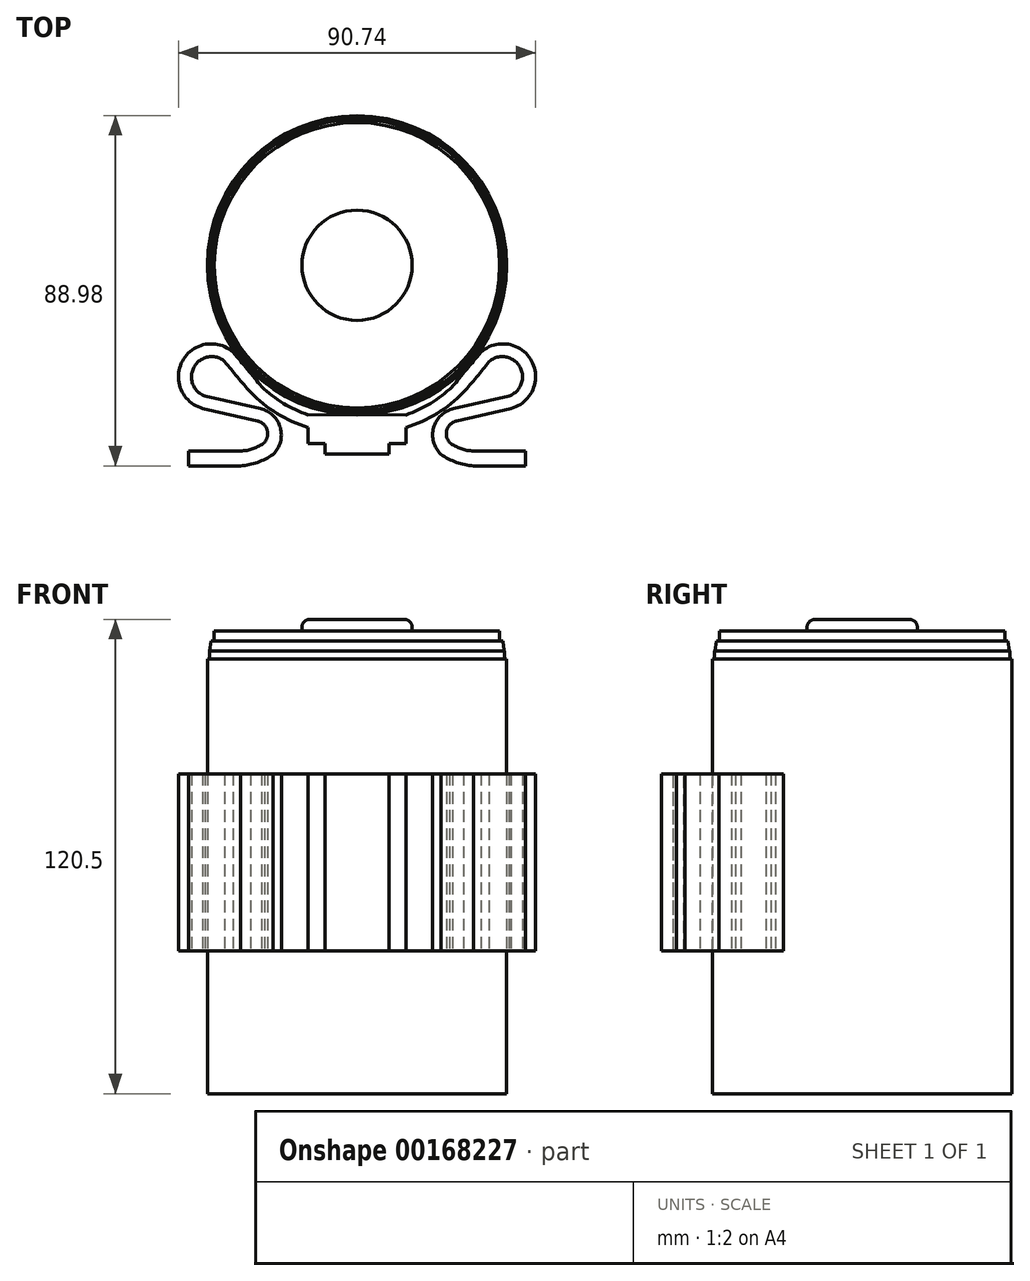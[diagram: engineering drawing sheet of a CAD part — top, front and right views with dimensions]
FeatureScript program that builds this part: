
annotation { "Feature Type Name" : "Feature", "Feature Type Description" : "" }
export const myFeature = defineFeature(function(context is Context, id is Id, definition is map)
    precondition{}
    {
        {
            var Q0;
            Q0=qCreatedBy(makeId("Top.planeOp"),FACE);
            var sketch = newSketch(context, id + "F0", { "sketchPlane" : qUnion([Q0])});
            skLineSegment(sketch, "E0", {"start": v(-45, 31.85) * mm, "end": v(-45, -23.43) * mm, "construction": true});
            skLineSegment(sketch, "E1", {"start": v(45, 35.82) * mm, "end": v(45, -24.86) * mm, "construction": true});
            skLineSegment(sketch, "E2", {"start": v(0, 45.7) * mm, "end": v(0, -31.06) * mm, "construction": true});
            skLineSegment(sketch, "E3", {"start": v(-42.56, 0.72) * mm, "end": v(-29.8, 0.72) * mm});
            skLineSegment(sketch, "E4", {"start": v(-29.8, 0.72) * mm, "end": v(-29.8, 1.26) * mm});
            skLineSegment(sketch, "E5", {"start": v(-29.8, 1.26) * mm, "end": v(-24.48, 2.8) * mm});
            skLineSegment(sketch, "E6", {"start": v(-24.47, 15.44) * mm, "end": v(-38.8, 18.71) * mm});
            skLineSegment(sketch, "E7", {"start": v(-33.58, 27.47) * mm, "end": v(-31.38, 25.18) * mm});
            skLineSegment(sketch, "E8", {"start": v(-3.53, 9.3) * mm, "end": v(0, 9.32) * mm});
            skLineSegment(sketch, "E9", {"start": v(-42.56, 0.72) * mm, "end": v(-42.4, 5.06) * mm});
            skLineSegment(sketch, "E10", {"start": v(-29.62, 4.65) * mm, "end": v(-25.37, 5.88) * mm});
            skLineSegment(sketch, "E11", {"start": v(-25.37, 12.36) * mm, "end": v(-39.82, 15.66) * mm});
            skLineSegment(sketch, "E12", {"start": v(-31.4, 29.83) * mm, "end": v(-29.25, 27.58) * mm});
            skLineSegment(sketch, "E13", {"start": v(-5.2, 12.4) * mm, "end": v(0, 12.4) * mm});
            skLineSegment(sketch, "E14", {"start": v(0, 12.4) * mm, "end": v(0, 9.32) * mm});
            skPoint(sketch, "E14.endSnap0", {"position": v(0, 9.32) * mm});
            skPoint(sketch, "E15.orphan", {"position": v(3.53, 9.32) * mm});
            skLineSegment(sketch, "E16", {"start": v(-29.62, 4.65) * mm, "end": v(-42.4, 5.06) * mm});
            skPoint(sketch, "E17.visualSharp", {"position": v(-24.47, 2.8) * mm});
            skArc(sketch, "E18", {"start": v(-24.47, 2.8) * mm, "mid": v(-19.43, 9.12) * mm, "end": v(-24.47, 15.44) * mm});
            skArc(sketch, "E19", {"start": v(-25.37, 5.88) * mm, "mid": v(-22.63, 9.12) * mm, "end": v(-25.37, 12.36) * mm});
            skArc(sketch, "E20", {"start": v(-33.58, 27.47) * mm, "mid": v(-41.4, 26.2) * mm, "end": v(-38.8, 18.71) * mm});
            skArc(sketch, "E21", {"start": v(-31.4, 29.83) * mm, "mid": v(-44.17, 27.83) * mm, "end": v(-39.82, 15.66) * mm});
            skArc(sketch, "E22", {"start": v(-31.38, 25.18) * mm, "mid": v(-19.45, 13.74) * mm, "end": v(-3.53, 9.3) * mm});
            skArc(sketch, "E23", {"start": v(-29.25, 27.58) * mm, "mid": v(-19.08, 17.04) * mm, "end": v(-5.2, 12.4) * mm});
            skLineSegment(sketch, "E24", {"start": v(-72.69, 0) * mm, "end": v(55.3, 0) * mm, "construction": true});
            skLineSegment(sketch, "E25.MirrorCS", {"start": v(5.2, 12.4) * mm, "end": v(0, 12.4) * mm});
            skLineSegment(sketch, "E26.MirrorCS", {"start": v(3.53, 9.3) * mm, "end": v(0, 9.32) * mm});
            skArc(sketch, "E27.MirrorCS", {"start": v(31.38, 25.18) * mm, "mid": v(19.45, 13.74) * mm, "end": v(3.53, 9.3) * mm});
            skArc(sketch, "E28.MirrorCS", {"start": v(29.25, 27.58) * mm, "mid": v(19.08, 17.04) * mm, "end": v(5.2, 12.4) * mm});
            skLineSegment(sketch, "E29.MirrorCS", {"start": v(31.4, 29.83) * mm, "end": v(29.25, 27.58) * mm});
            skLineSegment(sketch, "E30.MirrorCS", {"start": v(33.58, 27.47) * mm, "end": v(31.38, 25.18) * mm});
            skArc(sketch, "E31.MirrorCS", {"start": v(31.4, 29.83) * mm, "mid": v(44.17, 27.83) * mm, "end": v(39.82, 15.66) * mm});
            skArc(sketch, "E32.MirrorCS", {"start": v(33.58, 27.47) * mm, "mid": v(41.4, 26.2) * mm, "end": v(38.8, 18.71) * mm});
            skLineSegment(sketch, "E33.MirrorCS", {"start": v(24.47, 15.44) * mm, "end": v(38.8, 18.71) * mm});
            skLineSegment(sketch, "E34.MirrorCS", {"start": v(25.37, 12.36) * mm, "end": v(39.82, 15.66) * mm});
            skArc(sketch, "E35.MirrorCS", {"start": v(25.37, 5.88) * mm, "mid": v(22.63, 9.12) * mm, "end": v(25.37, 12.36) * mm});
            skArc(sketch, "E36.MirrorCS", {"start": v(24.47, 2.8) * mm, "mid": v(19.43, 9.12) * mm, "end": v(24.47, 15.44) * mm});
            skLineSegment(sketch, "E37.MirrorCS", {"start": v(29.8, 1.26) * mm, "end": v(24.48, 2.8) * mm});
            skLineSegment(sketch, "E38.MirrorCS", {"start": v(29.62, 4.65) * mm, "end": v(25.37, 5.88) * mm});
            skLineSegment(sketch, "E39.MirrorCS", {"start": v(29.62, 4.65) * mm, "end": v(42.4, 5.06) * mm});
            skLineSegment(sketch, "E40.MirrorCS", {"start": v(42.56, 0.72) * mm, "end": v(42.4, 5.06) * mm});
            skLineSegment(sketch, "E41.MirrorCS", {"start": v(42.56, 0.72) * mm, "end": v(29.8, 0.72) * mm});
            skLineSegment(sketch, "E42.MirrorCS", {"start": v(29.8, 0.72) * mm, "end": v(29.8, 1.26) * mm});
            skSolve(sketch);
        }
        {
            var Q0;
            Q0=qCreatedBy(makeId("Top.planeOp"),FACE);
            var sketch = newSketch(context, id + "F1", { "sketchPlane" : qUnion([Q0])});
            skLineSegment(sketch, "E43.bottom", {"start": v(-42.76, 0.96) * mm, "end": v(-29.61, 0.96) * mm});
            skLineSegment(sketch, "E43.top", {"start": v(-42.76, 4.77) * mm, "end": v(-29.61, 4.77) * mm});
            skLineSegment(sketch, "E43.left", {"start": v(-42.76, 0.96) * mm, "end": v(-42.76, 4.77) * mm});
            skArc(sketch, "E44", {"start": v(-23.5, 6.93) * mm, "mid": v(-22.86, 10.17) * mm, "end": v(-25.3, 12.4) * mm});
            skArc(sketch, "E45", {"start": v(-21.32, 3.9) * mm, "mid": v(-19.47, 10.68) * mm, "end": v(-24.56, 15.52) * mm});
            skLineSegment(sketch, "E46", {"start": v(-24.56, 15.52) * mm, "end": v(-38.6, 18.7) * mm});
            skLineSegment(sketch, "E47", {"start": v(-25.3, 12.4) * mm, "end": v(-39.18, 15.57) * mm});
            skArc(sketch, "E48", {"start": v(-29.61, 0.96) * mm, "mid": v(-25.26, 1.86) * mm, "end": v(-21.32, 3.9) * mm});
            skArc(sketch, "E49", {"start": v(-29.61, 4.77) * mm, "mid": v(-26.37, 5.33) * mm, "end": v(-23.5, 6.93) * mm});
            skArc(sketch, "E50", {"start": v(-33.6, 27.5) * mm, "mid": v(-41.39, 26.11) * mm, "end": v(-38.6, 18.7) * mm});
            skArc(sketch, "E51", {"start": v(-31.47, 29.85) * mm, "mid": v(-44.37, 27.59) * mm, "end": v(-39.18, 15.57) * mm});
            skArc(sketch, "E52", {"start": v(-24.2, 21.1) * mm, "mid": v(-27.82, 25.49) * mm, "end": v(-31.47, 29.85) * mm});
            skArc(sketch, "E53", {"start": v(-33.6, 27.5) * mm, "mid": v(-30.4, 23.53) * mm, "end": v(-27.05, 19.68) * mm});
            skArc(sketch, "E54", {"start": v(-24.2, 21.1) * mm, "mid": v(-13.04, 14.14) * mm, "end": v(0, 12.41) * mm});
            skArc(sketch, "E55", {"start": v(-27.05, 19.68) * mm, "mid": v(-14.68, 11.48) * mm, "end": v(0, 9.32) * mm});
            skLineSegment(sketch, "E56.0", {"start": v(0, 45.7) * mm, "end": v(0, -31.06) * mm, "construction": true});
            skArc(sketch, "E57.MirrorCS", {"start": v(23.5, 6.93) * mm, "mid": v(22.86, 10.17) * mm, "end": v(25.3, 12.4) * mm});
            skArc(sketch, "E58.MirrorCS", {"start": v(31.47, 29.85) * mm, "mid": v(44.37, 27.59) * mm, "end": v(39.18, 15.57) * mm});
            skArc(sketch, "E59.MirrorCS", {"start": v(24.2, 21.1) * mm, "mid": v(13.04, 14.14) * mm, "end": v(0, 12.41) * mm});
            skLineSegment(sketch, "E60.MirrorCS", {"start": v(24.56, 15.52) * mm, "end": v(38.6, 18.7) * mm});
            skArc(sketch, "E61.MirrorCS", {"start": v(24.2, 21.1) * mm, "mid": v(27.82, 25.49) * mm, "end": v(31.47, 29.85) * mm});
            skArc(sketch, "E62.MirrorCS", {"start": v(33.6, 27.5) * mm, "mid": v(41.39, 26.11) * mm, "end": v(38.6, 18.7) * mm});
            skArc(sketch, "E63.MirrorCS", {"start": v(27.05, 19.68) * mm, "mid": v(14.68, 11.48) * mm, "end": v(0, 9.32) * mm});
            skArc(sketch, "E64.MirrorCS", {"start": v(21.32, 3.9) * mm, "mid": v(19.47, 10.68) * mm, "end": v(24.56, 15.52) * mm});
            skArc(sketch, "E65.MirrorCS", {"start": v(29.61, 4.77) * mm, "mid": v(26.37, 5.33) * mm, "end": v(23.5, 6.93) * mm});
            skArc(sketch, "E66.MirrorCS", {"start": v(33.6, 27.5) * mm, "mid": v(30.4, 23.53) * mm, "end": v(27.05, 19.68) * mm});
            skLineSegment(sketch, "E67.MirrorCS", {"start": v(25.3, 12.4) * mm, "end": v(39.18, 15.57) * mm});
            skArc(sketch, "E68.MirrorCS", {"start": v(29.61, 0.96) * mm, "mid": v(25.26, 1.86) * mm, "end": v(21.32, 3.9) * mm});
            skLineSegment(sketch, "E69.MirrorCS", {"start": v(42.76, 4.77) * mm, "end": v(29.61, 4.77) * mm});
            skLineSegment(sketch, "E70.MirrorCS", {"start": v(42.76, 0.96) * mm, "end": v(29.61, 0.96) * mm});
            skLineSegment(sketch, "E71.MirrorCS", {"start": v(42.76, 0.96) * mm, "end": v(42.76, 4.77) * mm});
            skSolve(sketch);
        }
        {
            var Q0;
            Q0 = qSketchRegion(id + "F1", true);
            extrude(context, id + "F2", {"entities" : qUnion([Q0]), "depth" : 45 * mm});
        }
        {
            var Q0;
            Q0=qCreatedBy(makeId("Top.planeOp"),FACE);
            cPlane(context, id + "F3", {"entities" : qUnion([Q0]), "cplaneType" : CPlaneType.OFFSET, "offset" : 19 * mm, "width" : 150 * mm, "height" : 150 * mm});
        }
        {
            var Q0;
            Q0=qCreatedBy(id+"F3.planeOp",FACE);
            var sketch = newSketch(context, id + "F4", { "sketchPlane" : qUnion([Q0])});
            skCircle(sketch, "E72", {"center": v(0, 51.94) * mm, "radius": 38 * mm});
            skSolve(sketch);
        }
        {
            var Q0;
            Q0 = qSketchRegion(id + "F4", true);
            extrude(context, id + "F5", {"entities" : qUnion([Q0]), "endBound" : BoundingType.SYMMETRIC, "depth" : 110.5 * mm});
        }
        {
            var Q0;
            Q0=makeQuery(id+"F2.opExtrude","CAP_FACE",FACE,{"disambiguationData":[OSD([sQuery(id+"F1.wireOp",EDGE,"E43.bottom"),sQuery(id+"F1.wireOp",EDGE,"E43.top"),sQuery(id+"F1.wireOp",EDGE,"E43.left"),sQuery(id+"F1.wireOp",EDGE,"E44"),sQuery(id+"F1.wireOp",EDGE,"E45"),sQuery(id+"F1.wireOp",EDGE,"E46"),sQuery(id+"F1.wireOp",EDGE,"E47"),sQuery(id+"F1.wireOp",EDGE,"E48"),sQuery(id+"F1.wireOp",EDGE,"E49"),sQuery(id+"F1.wireOp",EDGE,"E50"),sQuery(id+"F1.wireOp",EDGE,"E51"),sQuery(id+"F1.wireOp",EDGE,"E52"),sQuery(id+"F1.wireOp",EDGE,"E53"),sQuery(id+"F1.wireOp",EDGE,"E54"),sQuery(id+"F1.wireOp",EDGE,"E55"),sQuery(id+"F1.wireOp",EDGE,"E58.MirrorCS"),sQuery(id+"F1.wireOp",EDGE,"E59.MirrorCS"),sQuery(id+"F1.wireOp",EDGE,"E60.MirrorCS"),sQuery(id+"F1.wireOp",EDGE,"E61.MirrorCS"),sQuery(id+"F1.wireOp",EDGE,"E62.MirrorCS"),sQuery(id+"F1.wireOp",EDGE,"E63.MirrorCS"),sQuery(id+"F1.wireOp",EDGE,"E66.MirrorCS"),sQuery(id+"F1.wireOp",EDGE,"E67.MirrorCS"),sQuery(id+"F1.wireOp",EDGE,"E64.MirrorCS"),sQuery(id+"F1.wireOp",EDGE,"E68.MirrorCS"),sQuery(id+"F1.wireOp",EDGE,"E69.MirrorCS"),sQuery(id+"F1.wireOp",EDGE,"E65.MirrorCS"),sQuery(id+"F1.wireOp",EDGE,"E70.MirrorCS"),sQuery(id+"F1.wireOp",EDGE,"E71.MirrorCS"),sQuery(id+"F1.wireOp",EDGE,"E57.MirrorCS")])],"isStart":false});
            var sketch = newSketch(context, id + "F6", { "sketchPlane" : qUnion([Q0])});
            skLineSegment(sketch, "E73.bottom", {"start": v(12.43, 13.93) * mm, "end": v(-12.43, 13.95) * mm});
            skLineSegment(sketch, "E73.left", {"start": v(12.43, 13.93) * mm, "end": v(12.43, 6.69) * mm});
            skLineSegment(sketch, "E73.right", {"start": v(-12.43, 13.95) * mm, "end": v(-12.43, 6.69) * mm});
            skPoint(sketch, "E73.middle", {"position": v(0, 9.32) * mm});
            skLineSegment(sketch, "E74", {"start": v(-12.43, 6.69) * mm, "end": v(-8.18, 6.69) * mm});
            skPoint(sketch, "E75.orphan", {"position": v(-12.43, 4.7) * mm});
            skPoint(sketch, "E76.orphan", {"position": v(12.43, 4.68) * mm});
            skLineSegment(sketch, "E77.left", {"start": v(8.18, 4.03) * mm, "end": v(8.18, 6.69) * mm});
            skLineSegment(sketch, "E77.right", {"start": v(-8.18, 4.03) * mm, "end": v(-8.18, 6.69) * mm});
            skPoint(sketch, "E77.middle", {"position": v(0, 7.03) * mm});
            skLineSegment(sketch, "E78.trimOffspring", {"start": v(8.18, 6.69) * mm, "end": v(12.43, 6.69) * mm});
            skPoint(sketch, "E77.top.end.orphan", {"position": v(-8.18, 10.03) * mm});
            skPoint(sketch, "E79.orphan", {"position": v(8.18, 10.03) * mm});
            skLineSegment(sketch, "E80", {"start": v(-8.18, 4.03) * mm, "end": v(8.18, 4.03) * mm});
            skSolve(sketch);
        }
        {
            var Q0;
            Q0 = qSketchRegion(id + "F6", true);
            extrude(context, id + "F7", {"entities" : qUnion([Q0]), "operationType" : NewBodyOperationType.ADD, "oppositeDirection" : true, "depth" : 45 * mm});
        }
        {
            var Q0;
            Q0=makeQuery(id+"F5.opExtrude","CAP_FACE",FACE,{"disambiguationData":[OSD([sQuery(id+"F4.wireOp",EDGE,"E72")])],"isStart":false});
            var sketch = newSketch(context, id + "F8", { "sketchPlane" : qUnion([Q0])});
            skCircle(sketch, "E81", {"center": v(0, 51.94) * mm, "radius": 37.5 * mm});
            skSolve(sketch);
        }
        {
            var Q0;
            Q0 = qSketchRegion(id + "F8", true);
            extrude(context, id + "F9", {"entities" : qUnion([Q0]), "depth" : 2 * mm});
        }
        {
            var Q0;
            Q0=makeQuery(id+"F9.opExtrude","CAP_FACE",FACE,{"disambiguationData":[OSD([sQuery(id+"F8.wireOp",EDGE,"E81")])],"isStart":false});
            var sketch = newSketch(context, id + "F10", { "sketchPlane" : qUnion([Q0])});
            skCircle(sketch, "E82", {"center": v(0, 51.94) * mm, "radius": 37.4 * mm});
            skSolve(sketch);
        }
        {
            var Q0;
            Q0 = qSketchRegion(id + "F10", true);
            extrude(context, id + "F11", {"entities" : qUnion([Q0]), "operationType" : NewBodyOperationType.ADD, "depth" : 2.5 * mm, "hasDraft" : true, "draftAngle" : 8 * degree, "draftPullDirection" : true, "hasSecondDirection" : true, "secondDirectionOppositeDirection" : true, "secondDirectionDepth" : 25 * mm});
        }
        {
            var Q0;
            Q0=makeQuery(id+"F11.opExtrude","CAP_FACE",FACE,{"disambiguationData":[OSD([sQuery(id+"F10.wireOp",EDGE,"E82")])],"isStart":false});
            var sketch = newSketch(context, id + "F12", { "sketchPlane" : qUnion([Q0])});
            skCircle(sketch, "E83", {"center": v(0, 51.94) * mm, "radius": 36.25 * mm});
            skSolve(sketch);
        }
        {
            var Q0;
            Q0 = qSketchRegion(id + "F12", true);
            extrude(context, id + "F13", {"entities" : qUnion([Q0]), "operationType" : NewBodyOperationType.ADD, "depth" : 2.5 * mm});
        }
        {
            var Q0;
            Q0=makeQuery(id+"F13.opExtrude","CAP_FACE",FACE,{"disambiguationData":[OSD([sQuery(id+"F12.wireOp",EDGE,"E83")])],"isStart":false});
            var sketch = newSketch(context, id + "F14", { "sketchPlane" : qUnion([Q0])});
            skCircle(sketch, "E84", {"center": v(0, 51.94) * mm, "radius": 14 * mm});
            skSolve(sketch);
        }
        {
            var Q0;
            Q0=makeQuery(id+"F14.imprint","IMPRINT",FACE,{"disambiguationData":[TD([[makeQuery(id+"F14.imprint","IMPRINT",EDGE,{"derivedFrom":sQuery(id+"F14.wireOp",EDGE,"E84")}),1.0]])]});
            var Q1;
            Q1=makeQuery(id+"F5.opExtrude","CAP_FACE",FACE,{"disambiguationData":[OSD([sQuery(id+"F4.wireOp",EDGE,"E72")])],"isStart":true});
            extrude(context, id + "F15", {"entities" : qUnion([Q0, Q1]), "operationType" : NewBodyOperationType.ADD, "depth" : 3 * mm});
        }
        {
            var Q0;
            Q0=makeQuery(id+"F15.opExtrude","CAP_FACE",FACE,{"disambiguationData":[OSD([sQuery(id+"F14.wireOp",EDGE,"E84")])],"isStart":false});
            fillet(context, id + "F16", {"entities" : qUnion([Q0]), "radius" : 2 * mm, "tangentPropagation" : true, "allowEdgeOverflow" : false});
        }
    });
